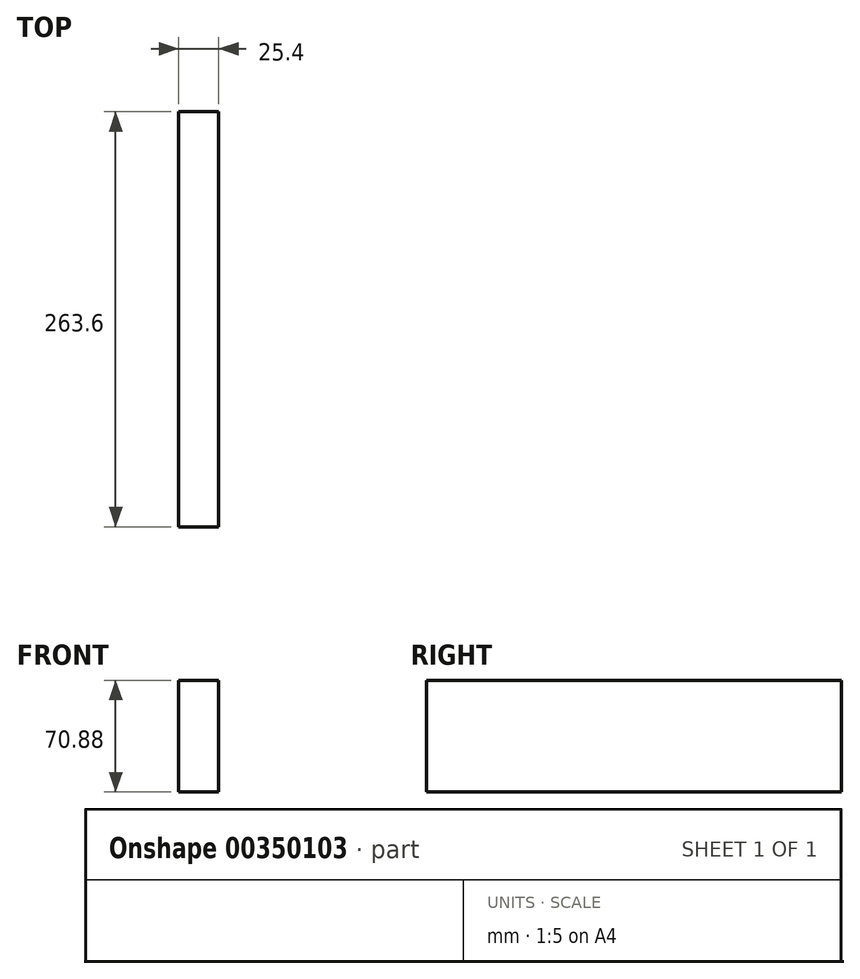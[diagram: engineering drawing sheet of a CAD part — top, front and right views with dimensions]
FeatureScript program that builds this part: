
annotation { "Feature Type Name" : "Feature", "Feature Type Description" : "" }
export const myFeature = defineFeature(function(context is Context, id is Id, definition is map)
    precondition{}
    {
        {
            var Q0;
            Q0=qCreatedBy(makeId("Right.planeOp"),FACE);
            var sketch = newSketch(context, id + "F0", { "sketchPlane" : qUnion([Q0])});
            skLineSegment(sketch, "E0.bottom", {"start": v(-114.6, -13.53) * mm, "end": v(149, -13.53) * mm});
            skLineSegment(sketch, "E0.top", {"start": v(-114.6, -84.41) * mm, "end": v(149, -84.41) * mm});
            skLineSegment(sketch, "E0.left", {"start": v(-114.6, -13.53) * mm, "end": v(-114.6, -84.41) * mm});
            skLineSegment(sketch, "E0.right", {"start": v(149, -13.53) * mm, "end": v(149, -84.41) * mm});
            skLineSegment(sketch, "E1.bottom", {"start": v(-107.9, 127.52) * mm, "end": v(-77.98, 127.52) * mm});
            skLineSegment(sketch, "E1.top", {"start": v(-107.9, 138.25) * mm, "end": v(-77.98, 138.25) * mm});
            skLineSegment(sketch, "E1.left", {"start": v(-107.9, 127.52) * mm, "end": v(-107.9, 138.25) * mm});
            skLineSegment(sketch, "E1.right", {"start": v(-77.98, 127.52) * mm, "end": v(-77.98, 138.25) * mm});
            skSolve(sketch);
        }
        {
            var Q0;
            Q0=makeQuery(id+"F0.imprint","IMPRINT",FACE,{"disambiguationData":[TD([[makeQuery(id+"F0.imprint","IMPRINT",EDGE,{"derivedFrom":sQuery(id+"F0.wireOp",EDGE,"E0.bottom")}),-1.0]])]});
            extrude(context, id + "F1", {"entities" : qUnion([Q0]), "depth" : 25.4 * mm});
        }
    });
